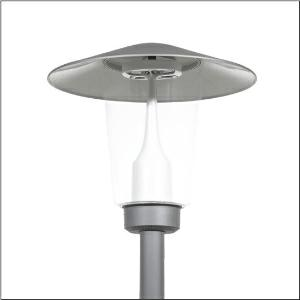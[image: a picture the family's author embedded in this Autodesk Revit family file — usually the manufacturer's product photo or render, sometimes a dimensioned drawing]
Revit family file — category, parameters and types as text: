
# Revit family: pilzleuchte_iq___st1_2a_5xa5235ef14hp_2efb
name_source: partatom
category: Lighting Fixtures
units: mm (PartAtom-declared; Revit-internal decimal feet)

## family parameters
Cut with Voids When Loaded = No
Host = Face
Light Source = No
Part Type = Normal
Room Calculation Point = No
Round Connector Dimension = Use Diameter
Shared = No

## types (1)
- --- (1 x LED, 4770 lm, 33.6 W, 3000K)
    Apparent Load = 34 VA
    CIE Flux Codes = 23 60 92 98 100
    Color Rendering = 70
    Color Temperature = 3000K
    Default Elevation = 1800 mm
    Description = Mushroom Luminaire iQ, mast luminaire, Module 540 iQ-SR, primary light control with 3 zone facetted reflector, of plastic, silver coated, highly specular, structured, primary optical cover: cover, of PMMA, transparent, light distribution: ST1.2a, light emission: direct distribution, primary light characteristic: asymmetric, installation type: post-top, LED, High Power LED, rated luminous flux: 4.770lm, luminous efficacy: 142lm/W, light colour: 730, colour temperature: 3000K, control gear: ECG iQ, control: presetting dimming logarithmic, Street-Remote, Auto-Match, Temp-Guard, Lumen-Switch, Night-Set, Smart-Wire, Light-Fading, Desk-Remote (wireless, voltage-free reading and setting of iQ features in the workshop via application-optimized NFC function/RFID function), optimised constant luminous flux control (CLO 2.0), with terminal, 6-pole, max. 2.5mm², mains connection: 230..240V, AC, 50/60Hz, start of lifetime: 34W, end of service life: 36W, reduction: 15W, luminaire housing, upper part, of glass-fibre reinforced polyester, coated, Siteco® metallic grey (DB 702S), diameter: 650mm, height: 586mm, spigot size: d x l = 76 x 70mm (post-top) | with reducer (optional accessory) 60 x 70mm, post-top mast mounting element, of diecast aluminium, coated, Siteco® metallic grey (DB 702S), Module 540 iQ-SR, traffic white (RAL 9016), equipment: Power, protection rating (complete): IP65, insulation class (complete): insulation class II (safety insulation), certification: CE, ENEC, VDE, packaging unit: 1 piece

Light Distribution: ST1.2a
    Height = 586 mm
    Lamp = 1 x LED
    Lamp Light Flux = 4770 lm
    Lamp Power = 33.6 W
    Lamp count = 1
    Length = 650 mm
    Luminous efficacy = 142 lm/W
    Manufacturer = Siteco
    ModVariant = No
    Model = 5XA5235EF14HP
    Number of Poles = 1
    OnlyDefault = Yes
    Power Factor = 1
    Product Name = Pilzleuchte iQ | ST1.2a
    Product group = mast luminaire | pylon top
    ProductGroupID = 6100
    Protection Class = Protection class II
    Protection Degree = IP 65
    RLX_Detail_Level = 1
    RLX_Emergency_Light_Flux = 0 lm
    RLX_Emergency_Type = 0
    RLX_Emergency_Type_DB = No
    RlxData = <blob elided: 51529 chars, md5=4d3eda6a>
    Socket = socket
    Standby Power = 0 W
    System Light Flux = 4770 lm
    System Power = 34 W
    Type Comments = factory setting: luminous flux: 100 % | dim-lin: 254 | 695 mA
    Type Image = l_1006077.jpg
    URL = http://relux.com
    VarID = @adj_146265
    Voltage = 0 V
    Weight = 0.00 kg
    Width = 0 mm  [stored 0 ft]

note: [stored X ft] marks values corroborated as IEEE doubles in the binary element streams (Revit-internal decimal feet)

## geometry (parser evidence)
native form markers: Blend x4, Sweep x11
no freeform markers — native parametric forms only
